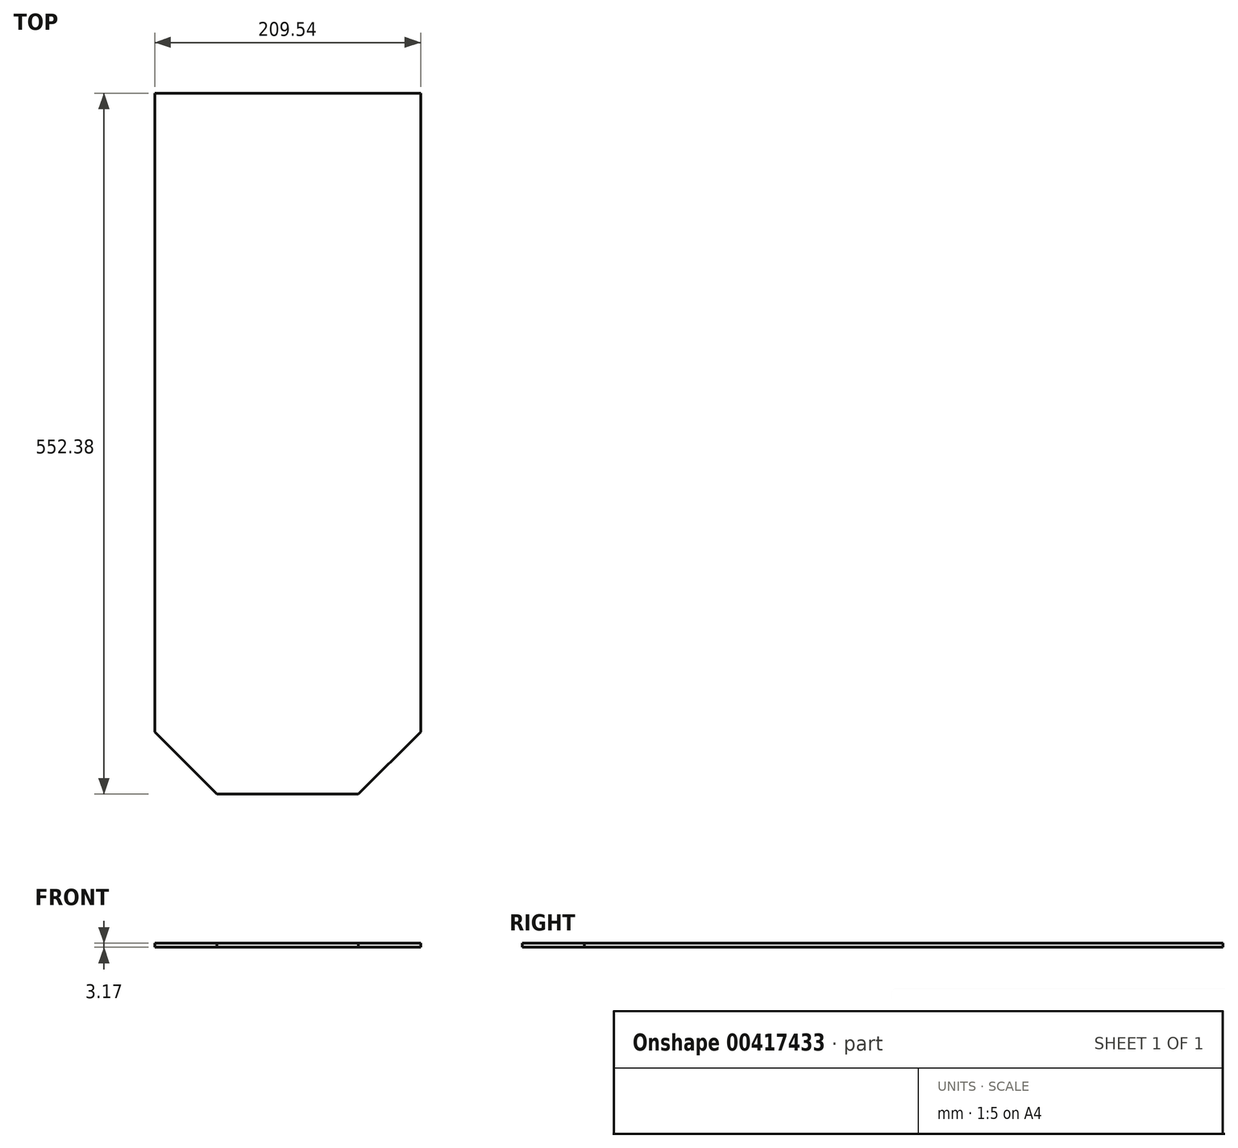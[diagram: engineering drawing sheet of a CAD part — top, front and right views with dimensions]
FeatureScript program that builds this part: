
annotation { "Feature Type Name" : "Feature", "Feature Type Description" : "" }
export const myFeature = defineFeature(function(context is Context, id is Id, definition is map)
    precondition{}
    {
        {
            var Q0;
            Q0=qCreatedBy(makeId("Top.planeOp"),FACE);
            var sketch = newSketch(context, id + "F0", { "sketchPlane" : qUnion([Q0])});
            skLineSegment(sketch, "E0.bottom", {"start": v(-104.77, 276.2) * mm, "end": v(104.77, 276.2) * mm});
            skLineSegment(sketch, "E0.top", {"start": v(-104.77, -276.2) * mm, "end": v(104.77, -276.2) * mm});
            skLineSegment(sketch, "E0.left", {"start": v(-104.77, 276.2) * mm, "end": v(-104.77, -276.2) * mm});
            skLineSegment(sketch, "E0.right", {"start": v(104.77, 276.2) * mm, "end": v(104.77, -276.2) * mm});
            skLineSegment(sketch, "E1", {"start": v(-104.77, -227.26) * mm, "end": v(-55.83, -276.2) * mm});
            skLineSegment(sketch, "E2", {"start": v(-55.83, -276.2) * mm, "end": v(-104.77, -276.2) * mm});
            skLineSegment(sketch, "E3", {"start": v(-104.77, -276.2) * mm, "end": v(-104.77, -227.26) * mm});
            skLineSegment(sketch, "E4", {"start": v(104.77, -227.26) * mm, "end": v(55.83, -276.2) * mm});
            skLineSegment(sketch, "E5", {"start": v(55.83, -276.2) * mm, "end": v(104.77, -276.2) * mm});
            skLineSegment(sketch, "E6", {"start": v(104.77, -227.26) * mm, "end": v(104.77, -276.2) * mm});
            skPoint(sketch, "E7", {"position": v(104.77, 0) * mm});
            skPoint(sketch, "E8", {"position": v(-104.77, 0) * mm});
            skPoint(sketch, "E9", {"position": v(0, 276.2) * mm});
            skPoint(sketch, "E10", {"position": v(0, -276.2) * mm});
            skSolve(sketch);
        }
        {
            var Q0;
            Q0=makeQuery(id+"F0.imprint","IMPRINT",FACE,{"disambiguationData":[TD([[makeQuery(id+"F0.imprint","IMPRINT",EDGE,{"derivedFrom":sQuery(id+"F0.wireOp",EDGE,"E0.bottom")}),-1.0]])]});
            extrude(context, id + "F1", {"entities" : qUnion([Q0]), "depth" : 3.17 * mm});
        }
    });
